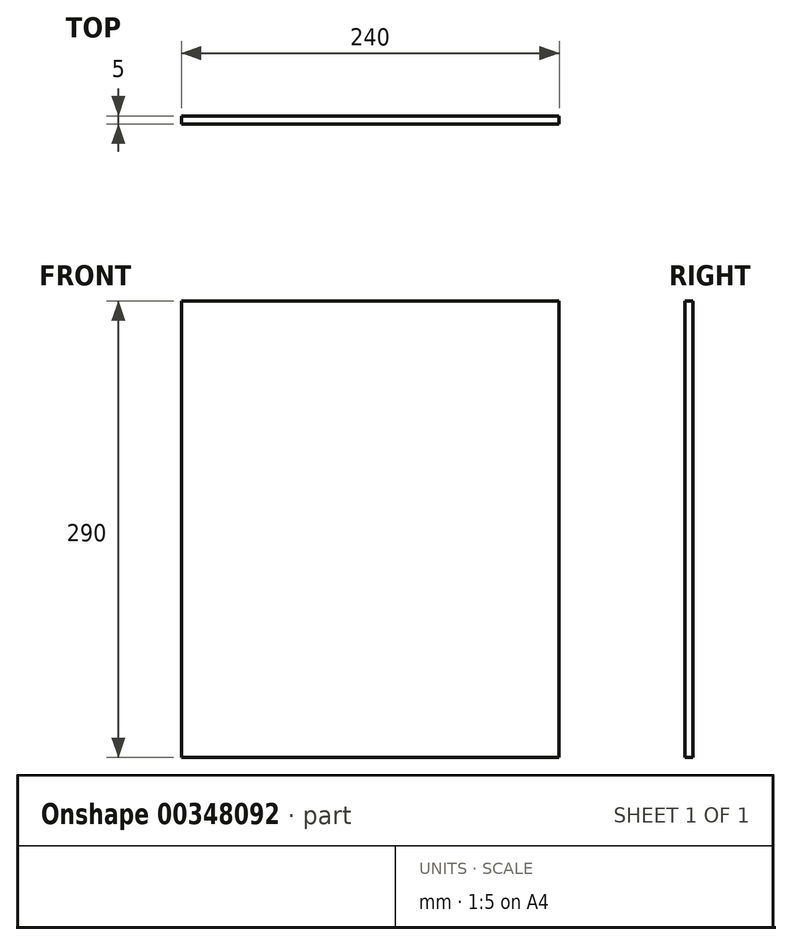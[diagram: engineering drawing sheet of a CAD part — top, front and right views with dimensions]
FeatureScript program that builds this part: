
annotation { "Feature Type Name" : "Feature", "Feature Type Description" : "" }
export const myFeature = defineFeature(function(context is Context, id is Id, definition is map)
    precondition{}
    {
        {
            var Q0;
            Q0=qCreatedBy(makeId("Front.planeOp"),FACE);
            var sketch = newSketch(context, id + "F0", { "sketchPlane" : qUnion([Q0])});
            skLineSegment(sketch, "E0.bottom", {"start": v(-158.57, 108.83) * mm, "end": v(81.43, 108.83) * mm});
            skLineSegment(sketch, "E0.top", {"start": v(-158.57, -181.17) * mm, "end": v(81.43, -181.17) * mm});
            skLineSegment(sketch, "E0.left", {"start": v(-158.57, 108.83) * mm, "end": v(-158.57, -181.17) * mm});
            skLineSegment(sketch, "E0.right", {"start": v(81.43, 108.83) * mm, "end": v(81.43, -181.17) * mm});
            skSolve(sketch);
        }
        {
            var Q0;
            Q0=makeQuery(id+"F0.imprint","IMPRINT",FACE,{"disambiguationData":[TD([[makeQuery(id+"F0.imprint","IMPRINT",EDGE,{"derivedFrom":sQuery(id+"F0.wireOp",EDGE,"E0.bottom")}),-1.0]])]});
            extrude(context, id + "F1", {"entities" : qUnion([Q0]), "depth" : 5 * mm});
        }
    });
